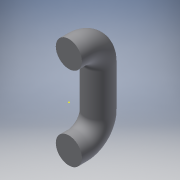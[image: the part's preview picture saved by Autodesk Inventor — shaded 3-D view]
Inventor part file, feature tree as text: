
AUTODESK INVENTOR PART (.ipt)
format: ipt  version: 2016 (Build 200138000, 138)  size: 144,896 bytes
history: native  units: mm
features: sketch x3, sweep x1
ambient origin geometry x8: Origin, YZ Plane, XZ Plane, XY Plane, X Axis, Y Axis, Z Axis, Center Point
bodies: Solid1 (feature_tree)
feature tree (4):
  sweep  "Sweep1"
  sketch  "Sketch3"  dims[d6=6.0mm d7=12.0mm d8=7.5mm d9=0.0mm d10=0.0mm]
  sketch  "Sketch1"  dims[d1=12.0mm d2=12.0mm]
  sketch  "Sketch2"  dims[d5=6.0mm]
